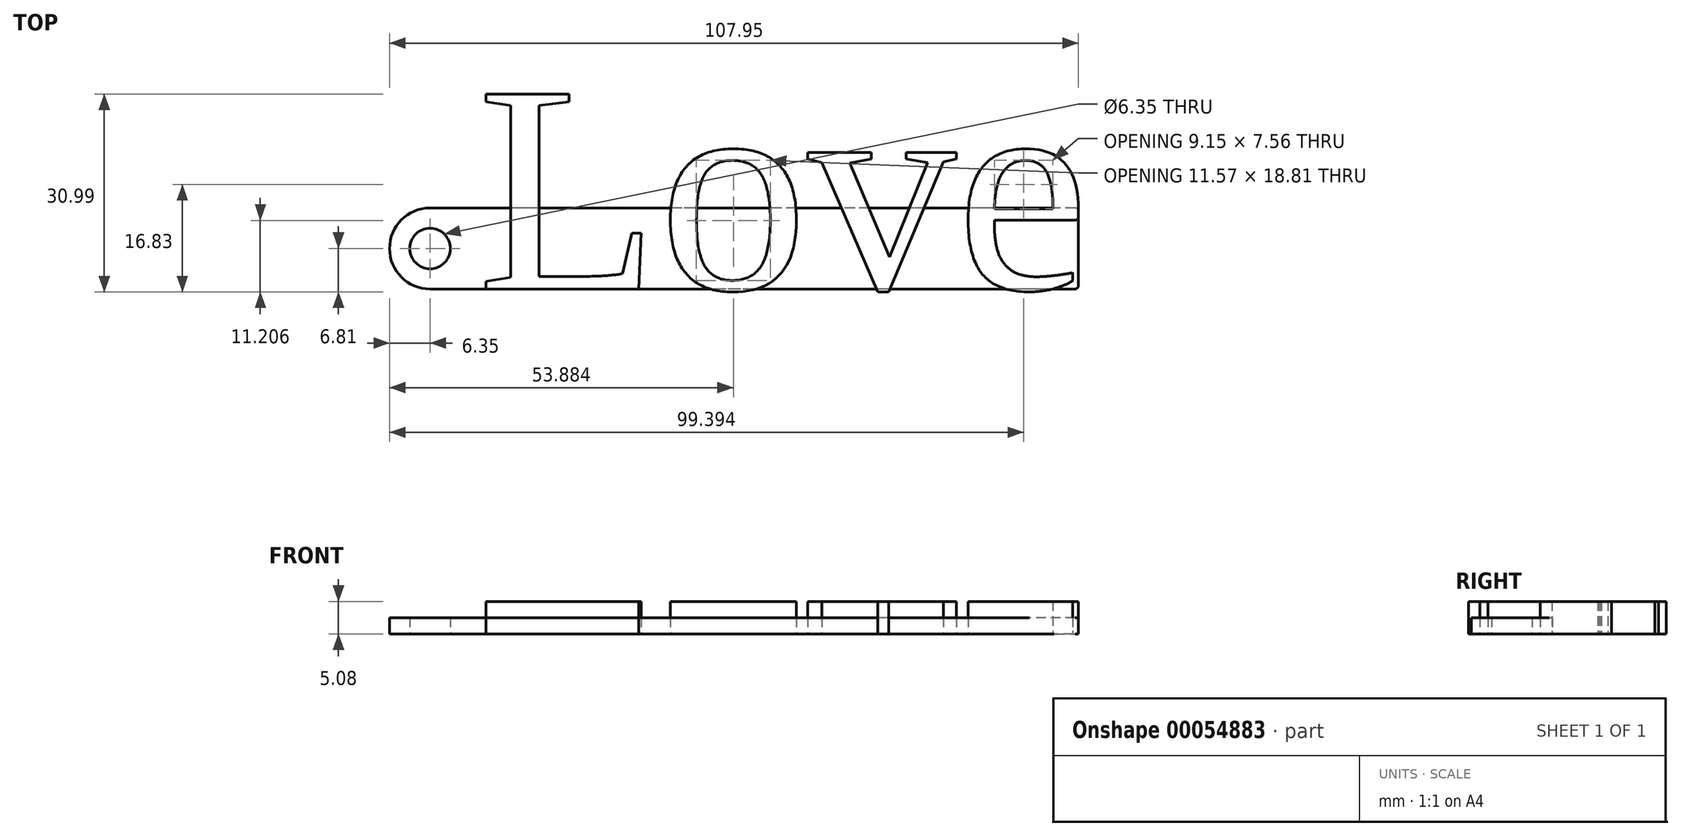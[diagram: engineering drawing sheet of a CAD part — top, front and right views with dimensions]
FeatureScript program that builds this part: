
annotation { "Feature Type Name" : "Feature", "Feature Type Description" : "" }
export const myFeature = defineFeature(function(context is Context, id is Id, definition is map)
    precondition{}
    {
        {
            var Q0;
            Q0=qCreatedBy(makeId("Top.planeOp"),FACE);
            var sketch = newSketch(context, id + "F0", { "sketchPlane" : qUnion([Q0])});
            skText(sketch, "E0", { "text": "Love", "fontName": "Tinos-Regular.ttf"});
            skLineSegment(sketch, "E1.right", {"start": v(0, 8.67) * mm, "end": v(0, 0) * mm});
            skLineSegment(sketch, "E2.left", {"start": v(0, 0) * mm, "end": v(0, 0) * mm});
            const initialGuessF0  = {"E0": [-0.0942, 0, 1, 0, 0.03357]};
            skSetInitialGuess(sketch, initialGuessF0);
            skSolve(sketch);
        }
        {
            var Q0;
            {var subQ5=sQuery(id+"F0.wireOp",EDGE,"E0.sketch_text.stroke-0");Q0=makeQuery(id+"F0.imprint","IMPRINT",FACE,{"disambiguationData":[TD([[makeQuery(id+"F0.imprint","IMPRINT",EDGE,{"derivedFrom":subQ5}),-1.0]])]});}
            var Q1;
            {var subQ8=sQuery(id+"F0.wireOp",EDGE,"E0.sketch_text.stroke-2");Q1=makeQuery(id+"F0.imprint","IMPRINT",FACE,{"disambiguationData":[TD([[makeQuery(id+"F0.imprint","IMPRINT",EDGE,{"derivedFrom":subQ8}),-1.0]])]});}
            var Q2;
            {var subQ5=sQuery(id+"F0.wireOp",EDGE,"E0.sketch_text.stroke-27");Q2=makeQuery(id+"F0.imprint","IMPRINT",FACE,{"disambiguationData":[TD([[makeQuery(id+"F0.imprint","IMPRINT",EDGE,{"derivedFrom":subQ5}),-1.0]])]});}
            var Q3;
            {var subQ6=sQuery(id+"F0.wireOp",EDGE,"E0.sketch_text.stroke-18");Q3=makeQuery(id+"F0.imprint","IMPRINT",FACE,{"disambiguationData":[TD([[makeQuery(id+"F0.imprint","IMPRINT",EDGE,{"derivedFrom":subQ6}),-1.0]])]});}
            var Q4;
            {var subQ0=sQuery(id+"F0.wireOp",EDGE,"E0.sketch_text.stroke-32");Q4=makeQuery(id+"F0.imprint","IMPRINT",FACE,{"disambiguationData":[TD([[makeQuery(id+"F0.imprint","IMPRINT",EDGE,{"derivedFrom":subQ0}),-1.0]])]});}
            var Q5;
            {var subQ3=sQuery(id+"F0.wireOp",EDGE,"E1.top");var subQ5=sQuery(id+"F0.wireOp",EDGE,"E0.sketch_text.stroke-31");var subQ6=makeQuery(id+"F0.imprint","INTERSECT",VERTEX,{"derivedFrom":[subQ5,subQ3]});Q5=makeQuery(id+"F0.imprint","IMPRINT",FACE,{"disambiguationData":[TD([[makeQuery(id+"F0.imprint","IMPRINT",EDGE,{"disambiguationData":[TD([[subQ6,-1.0]])],"derivedFrom":subQ5}),-1.0]])]});}
            var Q6;
            {var subQ0=sQuery(id+"F0.wireOp",EDGE,"E0.sketch_text.stroke-39");Q6=makeQuery(id+"F0.imprint","IMPRINT",FACE,{"disambiguationData":[TD([[makeQuery(id+"F0.imprint","IMPRINT",EDGE,{"derivedFrom":subQ0}),-1.0]])]});}
            var Q7;
            {var subQ0=sQuery(id+"F0.wireOp",EDGE,"E0.sketch_text.stroke-56");Q7=makeQuery(id+"F0.imprint","IMPRINT",FACE,{"disambiguationData":[TD([[makeQuery(id+"F0.imprint","IMPRINT",EDGE,{"derivedFrom":subQ0}),-1.0]])]});}
            var Q8;
            {var subQ1=sQuery(id+"F0.wireOp",EDGE,"E0.sketch_text.stroke-46");Q8=makeQuery(id+"F0.imprint","IMPRINT",FACE,{"disambiguationData":[TD([[makeQuery(id+"F0.imprint","IMPRINT",EDGE,{"derivedFrom":subQ1}),-1.0]])]});}
            extrude(context, id + "F1", {"entities" : qUnion([Q0, Q1, Q2, Q3, Q4, Q5, Q6, Q7, Q8]), "depth" : 5.08 * mm});
        }
        {
            var Q0;
            Q0=qCreatedBy(makeId("Top.planeOp"),FACE);
            var sketch = newSketch(context, id + "F2", { "sketchPlane" : qUnion([Q0])});
            skLineSegment(sketch, "E3.bottom", {"start": v(0, 0) * mm, "end": v(-101.6, 0) * mm});
            skLineSegment(sketch, "E3.top", {"start": v(0, 12.7) * mm, "end": v(-101.6, 12.7) * mm});
            skLineSegment(sketch, "E3.left", {"start": v(0, 0) * mm, "end": v(0, 12.7) * mm});
            skLineSegment(sketch, "E3.right", {"start": v(-101.6, 0) * mm, "end": v(-101.6, 12.7) * mm});
            skArc(sketch, "E4", {"start": v(-101.6, 12.7) * mm, "mid": v(-107.95, 6.35) * mm, "end": v(-101.6, 0) * mm});
            skCircle(sketch, "E5", {"center": v(-101.6, 6.35) * mm, "radius": 3.18 * mm});
            skSolve(sketch);
        }
        {
            var Q0;
            Q0=makeQuery(id+"F2.imprint","IMPRINT",FACE,{"disambiguationData":[TD([[makeQuery(id+"F2.imprint","IMPRINT",EDGE,{"derivedFrom":sQuery(id+"F2.wireOp",EDGE,"E3.bottom")}),-1.0]])]});
            var Q1;
            Q1=makeQuery(id+"F2.imprint","IMPRINT",FACE,{"disambiguationData":[TD([[makeQuery(id+"F2.imprint","IMPRINT",EDGE,{"derivedFrom":sQuery(id+"F2.wireOp",EDGE,"E3.right")}),1.0]])]});
            extrude(context, id + "F3", {"entities" : qUnion([Q0, Q1]), "depth" : 2.54 * mm});
        }
        {
            var Q0;
            Q0=makeQuery(id+"F3.opExtrude","SWEPT_EDGE",EDGE,{"disambiguationData":[OSD([sQuery(id+"F2.wireOp",EDGE,"E3.bottom"),sQuery(id+"F2.wireOp",EDGE,"E3.left")])]});
            var Q1;
            Q1=makeQuery(id+"F3.opExtrude","SWEPT_EDGE",EDGE,{"disambiguationData":[OSD([sQuery(id+"F2.wireOp",EDGE,"E3.top"),sQuery(id+"F2.wireOp",EDGE,"E3.left")])]});
            fillet(context, id + "F4", {"entities" : qUnion([Q0, Q1]), "radius" : 0.5 * mm, "tangentPropagation" : true, "allowEdgeOverflow" : false});
        }
        {
            var Q0;
            Q0=makeQuery(id+"F1.opExtrude","SWEPT_EDGE",EDGE,{"disambiguationData":[OSD([sQuery(id+"F0.wireOp",EDGE,"E0.sketch_text.stroke-59"),sQuery(id+"F0.wireOp",EDGE,"E0.sketch_text.stroke-60")])]});
            fillet(context, id + "F5", {"entities" : qUnion([Q0]), "radius" : 0.5 * mm, "tangentPropagation" : true, "allowEdgeOverflow" : false});
        }
    });
